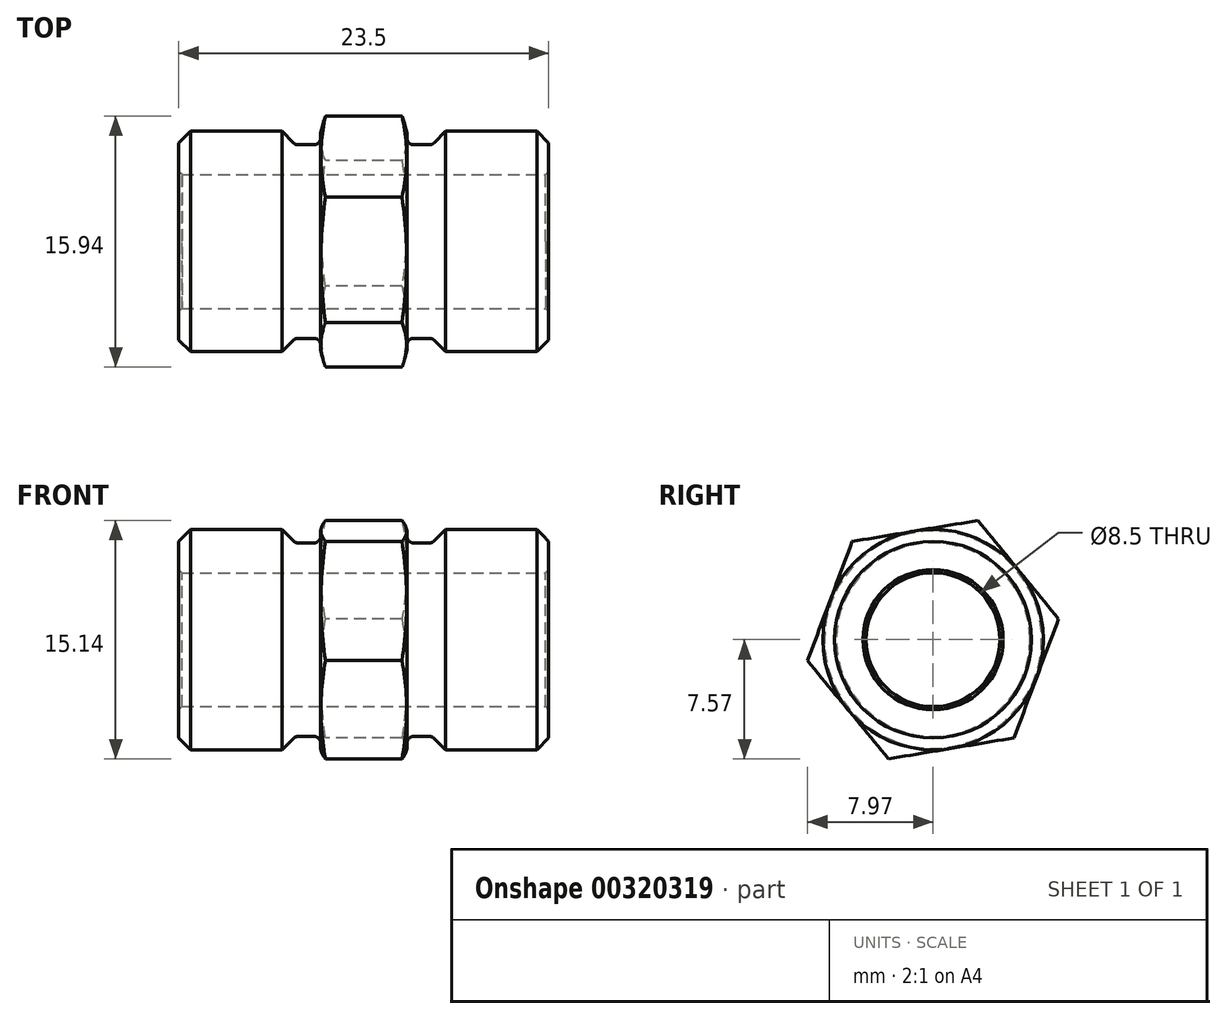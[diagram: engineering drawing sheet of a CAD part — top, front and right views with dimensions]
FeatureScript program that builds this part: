
annotation { "Feature Type Name" : "Feature", "Feature Type Description" : "" }
export const myFeature = defineFeature(function(context is Context, id is Id, definition is map)
    precondition{}
    {
        {
            var Q0;
            Q0=qCreatedBy(makeId("Front.planeOp"),FACE);
            var sketch = newSketch(context, id + "F0", { "sketchPlane" : qUnion([Q0])});
            skLineSegment(sketch, "E0", {"start": v(0, 0) * mm, "end": v(0, 6.15) * mm});
            skLineSegment(sketch, "E1", {"start": v(0, 6.15) * mm, "end": v(2.75, 6.15) * mm});
            skLineSegment(sketch, "E2", {"start": v(2.75, 6.15) * mm, "end": v(4.35, 6.15) * mm});
            skLineSegment(sketch, "E3", {"start": v(5.2, 7) * mm, "end": v(11.75, 7) * mm});
            skLineSegment(sketch, "E4", {"start": v(4.35, 6.15) * mm, "end": v(5.2, 7) * mm});
            skLineSegment(sketch, "E5", {"start": v(11.75, 7) * mm, "end": v(11.75, 0) * mm});
            skLineSegment(sketch, "E6", {"start": v(11.75, 0) * mm, "end": v(0, 0) * mm});
            skSolve(sketch);
        }
        {
            var Q0;
            Q0=makeQuery(id+"F0.imprint","IMPRINT",FACE,{"disambiguationData":[TD([[makeQuery(id+"F0.imprint","IMPRINT",EDGE,{"derivedFrom":sQuery(id+"F0.wireOp",EDGE,"E0")}),-1.0]])]});
            var Q1;
            Q1=sQuery(id+"F0.wireOp",EDGE,"E6");
            revolve(context, id + "F1", {"entities" : qUnion([Q0]), "axis" : qUnion([Q1]), "revolveType" : RevolveType.FULL});
        }
        {
            var Q0;
            Q0=makeQuery(id+"F1.opRevolve","SWEPT_EDGE",EDGE,{"disambiguationData":[OSD([sQuery(id+"F0.wireOp",EDGE,"E3"),sQuery(id+"F0.wireOp",EDGE,"E5")])]});
            chamfer(context, id + "F2", {"entities" : qUnion([Q0]), "chamferType" : ChamferType.OFFSET_ANGLE, "width" : 0.75 * mm, "oppositeDirection" : false, "angle" : 45 * degree, "tangentPropagation" : true});
        }
        {
            var Q0;
            Q0=makeQuery(id+"F1.opRevolve","SWEPT_EDGE",EDGE,{"disambiguationData":[OSD([sQuery(id+"F0.wireOp",EDGE,"E2"),sQuery(id+"F0.wireOp",EDGE,"E4")])]});
            fillet(context, id + "F3", {"entities" : qUnion([Q0]), "radius" : 0.4 * mm, "tangentPropagation" : true, "allowEdgeOverflow" : false});
        }
        {
            var Q0;
            Q0=makeQuery(id+"F1.opRevolve","SWEPT_BODY",BODY,{"disambiguationData":[OSD([sQuery(id+"F0.wireOp",EDGE,"E0"),sQuery(id+"F0.wireOp",EDGE,"E1"),sQuery(id+"F0.wireOp",EDGE,"E2"),sQuery(id+"F0.wireOp",EDGE,"E3"),sQuery(id+"F0.wireOp",EDGE,"E4"),sQuery(id+"F0.wireOp",EDGE,"E5"),sQuery(id+"F0.wireOp",EDGE,"E6")])]});
            var Q1;
            Q1=qCreatedBy(makeId("Front.planeOp"),FACE);
            mirror(context, id + "F4", {"operationType" : NewBodyOperationType.ADD, "entities" : qUnion([Q0]), "mirrorPlane" : qUnion([Q1])});
        }
        {
            var Q0;
            Q0=makeQuery(id+"F1.opRevolve","SWEPT_BODY",BODY,{"disambiguationData":[OSD([sQuery(id+"F0.wireOp",EDGE,"E0"),sQuery(id+"F0.wireOp",EDGE,"E1"),sQuery(id+"F0.wireOp",EDGE,"E2"),sQuery(id+"F0.wireOp",EDGE,"E3"),sQuery(id+"F0.wireOp",EDGE,"E4"),sQuery(id+"F0.wireOp",EDGE,"E5"),sQuery(id+"F0.wireOp",EDGE,"E6")])]});
            var Q1;
            Q1=qCreatedBy(makeId("Right.planeOp"),FACE);
            mirror(context, id + "F5", {"operationType" : NewBodyOperationType.ADD, "entities" : qUnion([Q0]), "mirrorPlane" : qUnion([Q1])});
        }
        {
            var Q0;
            Q0=qCreatedBy(makeId("Right.planeOp"),FACE);
            var sketch = newSketch(context, id + "F6", { "sketchPlane" : qUnion([Q0])});
            skCircle(sketch, "E7.cCircle", {"center": v(0, 0) * mm, "radius": 8.08 * mm, "construction": true});
            skLineSegment(sketch, "E7.0", {"start": v(-5.14, 6.24) * mm, "end": v(2.83, 7.57) * mm});
            skLineSegment(sketch, "E7.1", {"start": v(2.83, 7.57) * mm, "end": v(7.97, 1.33) * mm});
            skLineSegment(sketch, "E7.2", {"start": v(7.97, 1.33) * mm, "end": v(5.14, -6.24) * mm});
            skLineSegment(sketch, "E7.3", {"start": v(5.14, -6.24) * mm, "end": v(-2.83, -7.57) * mm});
            skLineSegment(sketch, "E7.4", {"start": v(-2.83, -7.57) * mm, "end": v(-7.97, -1.33) * mm});
            skLineSegment(sketch, "E7.5", {"start": v(-7.97, -1.33) * mm, "end": v(-5.14, 6.24) * mm});
            skSolve(sketch);
        }
        {
            var Q0;
            Q0 = qSketchRegion(id + "F6", true);
            extrude(context, id + "F7", {"entities" : qUnion([Q0]), "operationType" : NewBodyOperationType.ADD, "depth" : 2.75 * mm, "hasSecondDirection" : true, "secondDirectionOppositeDirection" : true, "secondDirectionDepth" : 2.75 * mm});
        }
        {
            var Q0;
            {var subQ0=makeQuery(id+"F1.opRevolve","SWEPT_FACE",FACE,{"disambiguationData":[OSD([sQuery(id+"F0.wireOp",EDGE,"E1"),sQuery(id+"F0.wireOp",EDGE,"E2")])]});Q0=makeQuery(id+"F7.boolean.opBoolean","INTERSECT",EDGE,{"derivedFrom":[makeQuery(id+"F5.boolean.opBoolean","MERGE",FACE,{"derivedFrom":[subQ0,makeQuery(id+"F5.opPattern","COPY",FACE,{"derivedFrom":subQ0,"instanceName":"1"})]}),makeQuery(id+"F7.opExtrude","CAP_FACE",FACE,{"disambiguationData":[OSD([sQuery(id+"F6.wireOp",EDGE,"E7.0"),sQuery(id+"F6.wireOp",EDGE,"E7.1"),sQuery(id+"F6.wireOp",EDGE,"E7.2"),sQuery(id+"F6.wireOp",EDGE,"E7.3"),sQuery(id+"F6.wireOp",EDGE,"E7.4"),sQuery(id+"F6.wireOp",EDGE,"E7.5")])],"isStart":true})]});}
            var Q1;
            {var subQ0=makeQuery(id+"F1.opRevolve","SWEPT_FACE",FACE,{"disambiguationData":[OSD([sQuery(id+"F0.wireOp",EDGE,"E1"),sQuery(id+"F0.wireOp",EDGE,"E2")])]});Q1=makeQuery(id+"F7.boolean.opBoolean","INTERSECT",EDGE,{"derivedFrom":[makeQuery(id+"F5.boolean.opBoolean","MERGE",FACE,{"derivedFrom":[subQ0,makeQuery(id+"F5.opPattern","COPY",FACE,{"derivedFrom":subQ0,"instanceName":"1"})]}),makeQuery(id+"F7.opExtrude","CAP_FACE",FACE,{"disambiguationData":[OSD([sQuery(id+"F6.wireOp",EDGE,"E7.0"),sQuery(id+"F6.wireOp",EDGE,"E7.1"),sQuery(id+"F6.wireOp",EDGE,"E7.2"),sQuery(id+"F6.wireOp",EDGE,"E7.3"),sQuery(id+"F6.wireOp",EDGE,"E7.4"),sQuery(id+"F6.wireOp",EDGE,"E7.5")])],"isStart":false})]});}
            fillet(context, id + "F8", {"entities" : qUnion([Q0, Q1]), "radius" : 0.4 * mm, "tangentPropagation" : true, "allowEdgeOverflow" : false});
        }
        {
            var Q0;
            Q0=qCreatedBy(makeId("Top.planeOp"),FACE);
            var sketch = newSketch(context, id + "F9", { "sketchPlane" : qUnion([Q0])});
            skLineSegment(sketch, "E8", {"start": v(-2.75, 6.9) * mm, "end": v(-2, 9.7) * mm});
            skLineSegment(sketch, "E9", {"start": v(-2, 9.7) * mm, "end": v(-5.52, 9.7) * mm});
            skLineSegment(sketch, "E10", {"start": v(-5.52, 9.7) * mm, "end": v(-2.75, 6.9) * mm});
            skLineSegment(sketch, "E11", {"start": v(-11.82, 0) * mm, "end": v(0, 0) * mm});
            skSolve(sketch);
        }
        {
            var Q0;
            Q0=makeQuery(id+"F9.imprint","IMPRINT",FACE,{"disambiguationData":[TD([[makeQuery(id+"F9.imprint","IMPRINT",EDGE,{"derivedFrom":sQuery(id+"F9.wireOp",EDGE,"E8")}),1.0]])]});
            var Q1;
            Q1=sQuery(id+"F9.wireOp",EDGE,"E11");
            revolve(context, id + "F10", {"entities" : qUnion([Q0]), "axis" : qUnion([Q1]), "revolveType" : RevolveType.FULL});
        }
        {
            var Q0;
            Q0=makeQuery(id+"F10.opRevolve","SWEPT_BODY",BODY,{"disambiguationData":[OSD([sQuery(id+"F9.wireOp",EDGE,"E8"),sQuery(id+"F9.wireOp",EDGE,"E9"),sQuery(id+"F9.wireOp",EDGE,"E10")])]});
            var Q1;
            Q1=qCreatedBy(makeId("Right.planeOp"),FACE);
            mirror(context, id + "F11", {"entities" : qUnion([Q0]), "mirrorPlane" : qUnion([Q1])});
        }
        {
            var Q0;
            Q0=makeQuery(id+"F10.opRevolve","SWEPT_BODY",BODY,{"disambiguationData":[OSD([sQuery(id+"F9.wireOp",EDGE,"E8"),sQuery(id+"F9.wireOp",EDGE,"E9"),sQuery(id+"F9.wireOp",EDGE,"E10")])]});
            var Q1;
            Q1=makeQuery(id+"F11.opPattern","COPY",BODY,{"derivedFrom":makeQuery(id+"F10.opRevolve","SWEPT_BODY",BODY,{"disambiguationData":[OSD([sQuery(id+"F9.wireOp",EDGE,"E8"),sQuery(id+"F9.wireOp",EDGE,"E9"),sQuery(id+"F9.wireOp",EDGE,"E10")])]}),"instanceName":"1"});
            var Q2;
            Q2=makeQuery(id+"F1.opRevolve","SWEPT_BODY",BODY,{"disambiguationData":[OSD([sQuery(id+"F0.wireOp",EDGE,"E0"),sQuery(id+"F0.wireOp",EDGE,"E1"),sQuery(id+"F0.wireOp",EDGE,"E2"),sQuery(id+"F0.wireOp",EDGE,"E3"),sQuery(id+"F0.wireOp",EDGE,"E4"),sQuery(id+"F0.wireOp",EDGE,"E5"),sQuery(id+"F0.wireOp",EDGE,"E6")])]});
            booleanBodies(context, id + "F12", {"operationType" : BooleanOperationType.SUBTRACTION, "tools" : qUnion([Q0, Q1]), "targets" : qUnion([Q2])});
        }
        {
            var Q0;
            Q0=makeQuery(id+"F1.opRevolve","SWEPT_FACE",FACE,{"disambiguationData":[OSD([sQuery(id+"F0.wireOp",EDGE,"E5")])]});
            var sketch = newSketch(context, id + "F13", { "sketchPlane" : qUnion([Q0])});
            skCircle(sketch, "E12", {"center": v(0, 0) * mm, "radius": 4.25 * mm});
            skSolve(sketch);
        }
        {
            var Q0;
            Q0=makeQuery(id+"F13.imprint","IMPRINT",FACE,{"disambiguationData":[TD([[makeQuery(id+"F13.imprint","IMPRINT",EDGE,{"derivedFrom":sQuery(id+"F13.wireOp",EDGE,"E12")}),1.0]])]});
            extrude(context, id + "F14", {"entities" : qUnion([Q0]), "operationType" : NewBodyOperationType.REMOVE, "oppositeDirection" : true, "depth" : 25 * mm, "hasSecondDirection" : true, "secondDirectionBound" : SecondDirectionBoundingType.THROUGH_ALL, "secondDirectionOppositeDirection" : false, "secondDirectionDepth" : 25 * mm});
        }
        {
            var Q0;
            Q0=makeQuery(id+"F14.boolean.opBoolean","INTERSECT",EDGE,{"derivedFrom":[makeQuery(id+"F1.opRevolve","SWEPT_FACE",FACE,{"disambiguationData":[OSD([sQuery(id+"F0.wireOp",EDGE,"E5")])]}),makeQuery(id+"F14.opExtrude","SWEPT_FACE",FACE,{"disambiguationData":[OSD([sQuery(id+"F13.wireOp",EDGE,"E12")])]})]});
            var Q1;
            Q1=makeQuery(id+"F14.boolean.opBoolean","INTERSECT",EDGE,{"derivedFrom":[makeQuery(id+"F5.opPattern","COPY",FACE,{"derivedFrom":makeQuery(id+"F1.opRevolve","SWEPT_FACE",FACE,{"disambiguationData":[OSD([sQuery(id+"F0.wireOp",EDGE,"E5")])]}),"instanceName":"1"}),makeQuery(id+"F14.opExtrude","SWEPT_FACE",FACE,{"disambiguationData":[OSD([sQuery(id+"F13.wireOp",EDGE,"E12")])]})]});
            chamfer(context, id + "F15", {"entities" : qUnion([Q0, Q1]), "chamferType" : ChamferType.OFFSET_ANGLE, "width" : 0.2 * mm, "oppositeDirection" : false, "angle" : 45 * degree, "tangentPropagation" : true});
        }
    });
